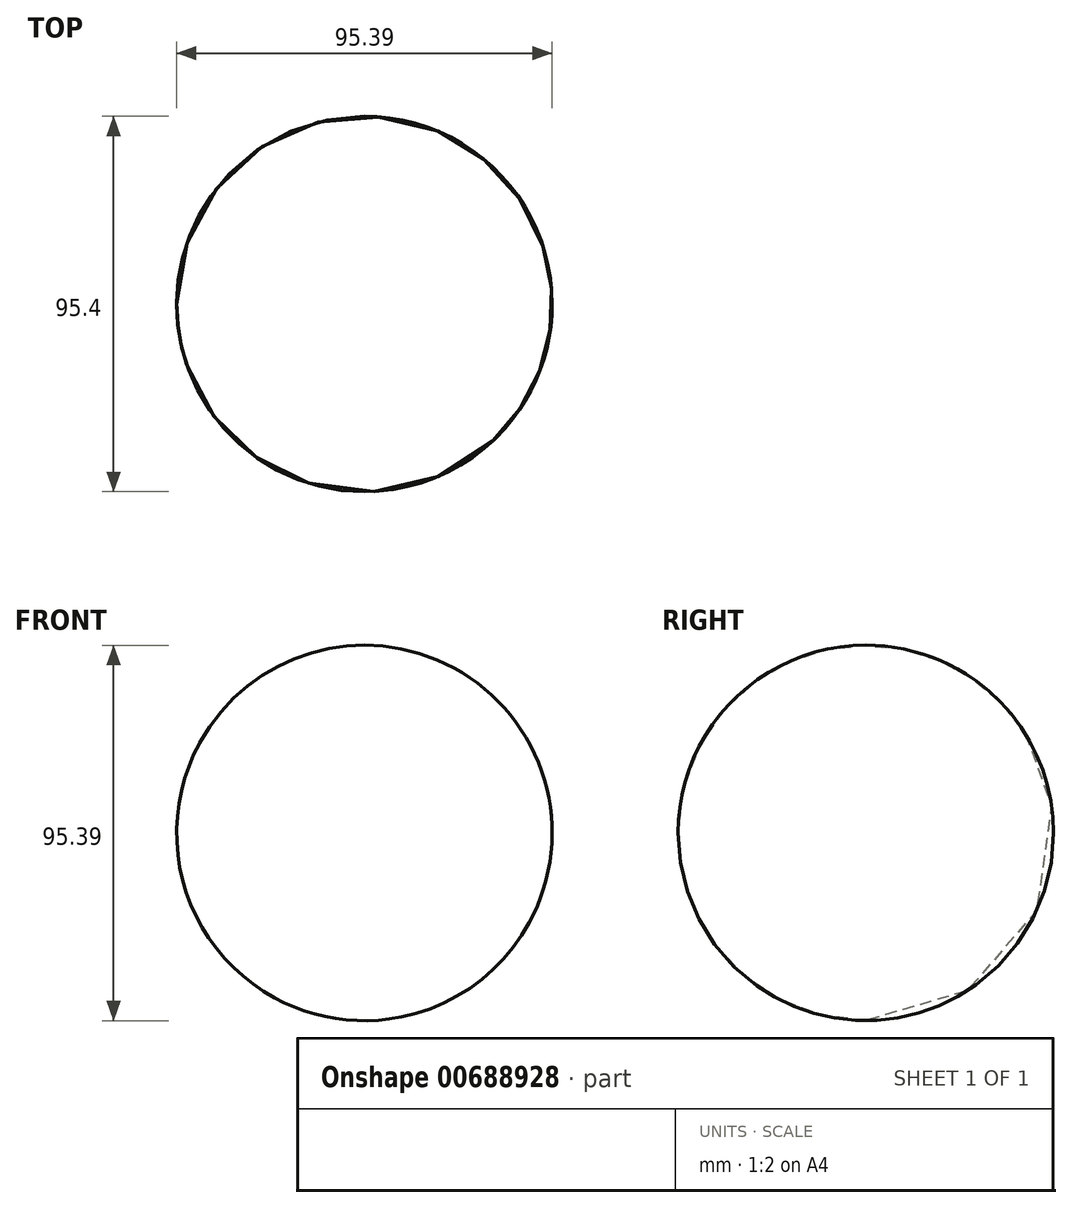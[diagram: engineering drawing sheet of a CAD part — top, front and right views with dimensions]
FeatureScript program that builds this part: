
annotation { "Feature Type Name" : "Feature", "Feature Type Description" : "" }
export const myFeature = defineFeature(function(context is Context, id is Id, definition is map)
    precondition{}
    {
        {
            var Q0;
            Q0=qCreatedBy(makeId("Front.planeOp"),FACE);
            var sketch = newSketch(context, id + "F0", { "sketchPlane" : qUnion([Q0])});
            skArc(sketch, "E0", {"start": v(41.88, -22.8) * mm, "mid": v(22.8, 41.88) * mm, "end": v(-41.87, 22.81) * mm});
            skLineSegment(sketch, "E1", {"start": v(-41.87, 22.81) * mm, "end": v(41.88, -22.8) * mm});
            skSolve(sketch);
        }
        {
            var Q0;
            Q0 = qSketchRegion(id + "F0", true);
            var Q1;
            Q1=sQuery(id+"F0.wireOp",EDGE,"E1");
            revolve(context, id + "F1", {"entities" : qUnion([Q0]), "axis" : qUnion([Q1]), "revolveType" : RevolveType.FULL});
        }
    });
